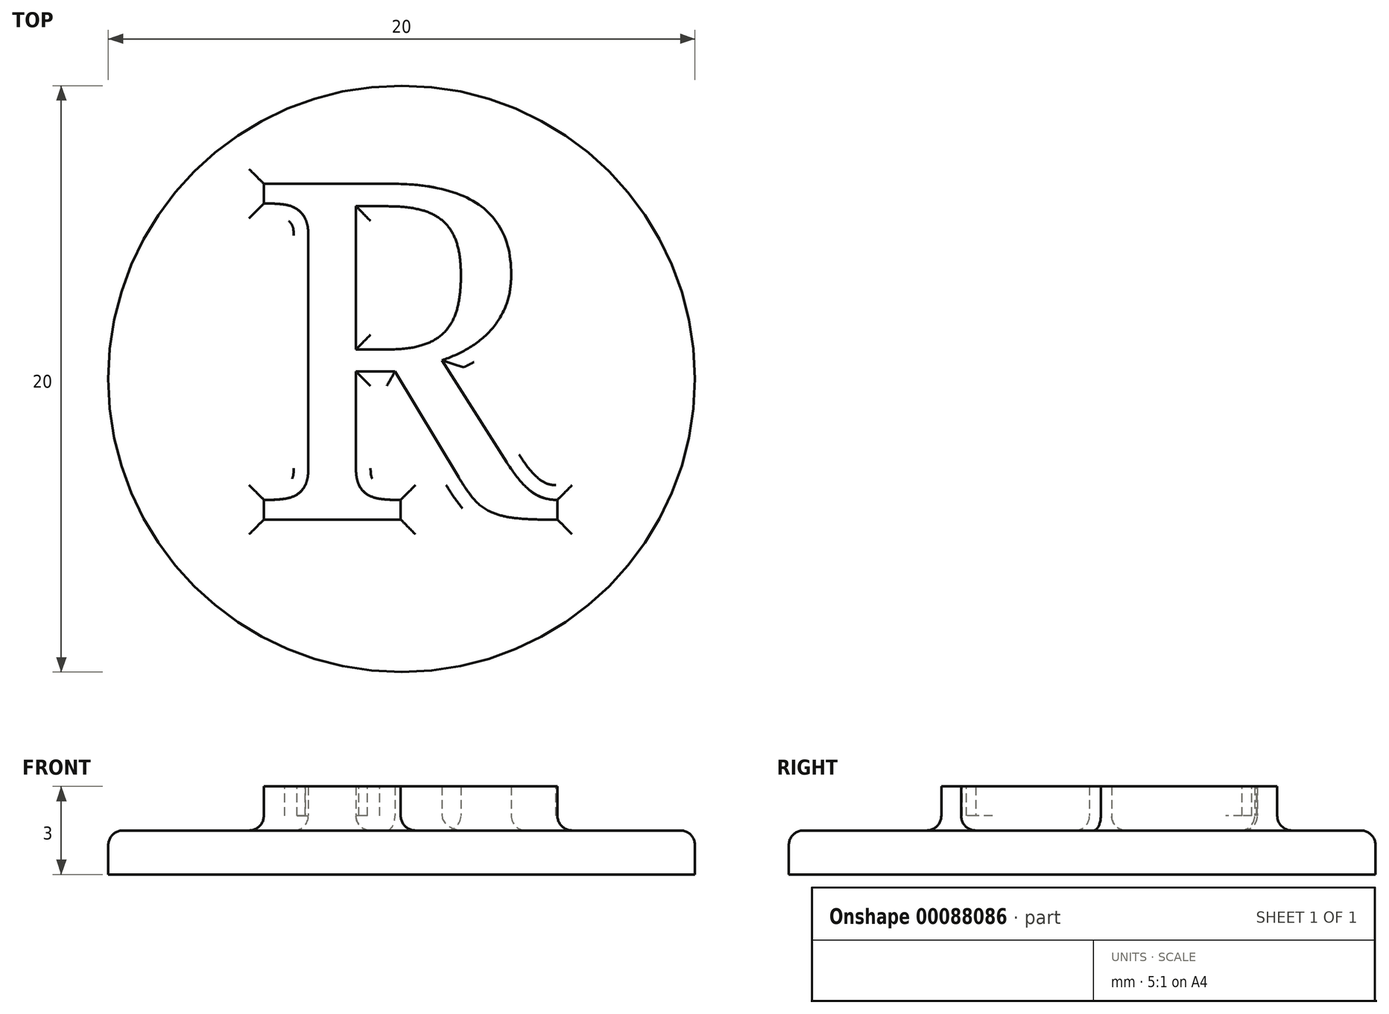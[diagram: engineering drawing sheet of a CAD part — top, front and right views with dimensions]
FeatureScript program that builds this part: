
annotation { "Feature Type Name" : "Feature", "Feature Type Description" : "" }
export const myFeature = defineFeature(function(context is Context, id is Id, definition is map)
    precondition{}
    {
        {
            var Q0;
            Q0=qCreatedBy(makeId("Top.planeOp"),FACE);
            var sketch = newSketch(context, id + "F0", { "sketchPlane" : qUnion([Q0])});
            skCircle(sketch, "E0", {"center": v(0, 0) * mm, "radius": 10 * mm});
            skSolve(sketch);
        }
        {
            var Q0;
            Q0=makeQuery(id+"F0.imprint","IMPRINT",FACE,{"disambiguationData":[TD([[makeQuery(id+"F0.imprint","IMPRINT",EDGE,{"derivedFrom":sQuery(id+"F0.wireOp",EDGE,"E0")}),1.0]])]});
            extrude(context, id + "F1", {"entities" : qUnion([Q0]), "depth" : 1.5 * mm});
        }
        {
            var Q0;
            Q0=makeQuery(id+"F1.opExtrude","CAP_FACE",FACE,{"disambiguationData":[OSD([sQuery(id+"F0.wireOp",EDGE,"E0")])],"isStart":false});
            var sketch = newSketch(context, id + "F2", { "sketchPlane" : qUnion([Q0])});
            skText(sketch, "E1", { "text": "R", "fontName": "NotoSerif-Regular.ttf"});
            skLineSegment(sketch, "E2", {"start": v(0, 0) * mm, "end": v(0, 6.74) * mm, "construction": true});
            const initialGuessF2  = {"E1": [-0.00531, -0.0048, 1, 0, 0.01155]};
            skSetInitialGuess(sketch, initialGuessF2);
            skSolve(sketch);
        }
        {
            var Q0;
            Q0 = qSketchRegion(id + "F2", true);
            extrude(context, id + "F3", {"entities" : qUnion([Q0]), "operationType" : NewBodyOperationType.ADD, "depth" : 1.5 * mm});
        }
        {
            var Q0;
            Q0=makeQuery(id+"F1.opExtrude","CAP_FACE",FACE,{"disambiguationData":[OSD([sQuery(id+"F0.wireOp",EDGE,"E0")])],"isStart":false});
            fillet(context, id + "F4", {"entities" : qUnion([Q0]), "radius" : .5 * mm, "tangentPropagation" : true, "allowEdgeOverflow" : false});
        }
    });
